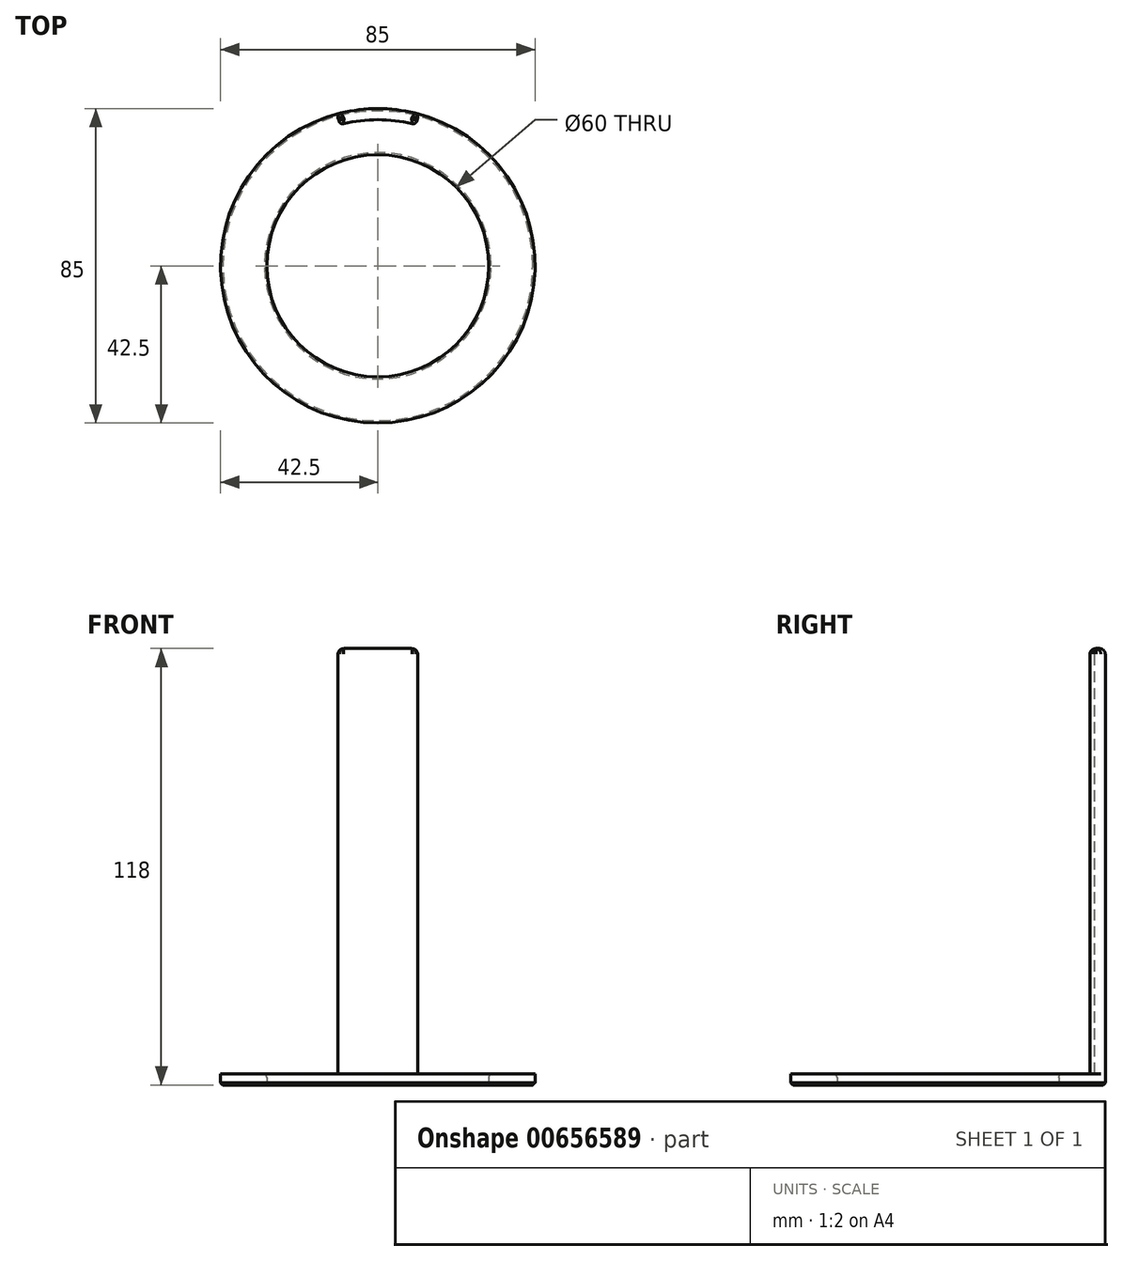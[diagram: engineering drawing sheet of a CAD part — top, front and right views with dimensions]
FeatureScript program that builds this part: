
annotation { "Feature Type Name" : "Feature", "Feature Type Description" : "" }
export const myFeature = defineFeature(function(context is Context, id is Id, definition is map)
    precondition{}
    {
        {
            var Q0;
            Q0=qCreatedBy(makeId("Front.planeOp"),FACE);
            var sketch = newSketch(context, id + "F0", { "sketchPlane" : qUnion([Q0])});
            skLineSegment(sketch, "E0", {"start": v(0, 0) * mm, "end": v(0, 66.8) * mm, "construction": true});
            skSolve(sketch);
        }
        {
            var Q0;
            Q0=qCreatedBy(makeId("Top.planeOp"),FACE);
            var sketch = newSketch(context, id + "F1", { "sketchPlane" : qUnion([Q0])});
            skCircle(sketch, "E1", {"center": v(0, 0) * mm, "radius": 42.5 * mm});
            skCircle(sketch, "E2", {"center": v(0, 0) * mm, "radius": 30 * mm});
            skSolve(sketch);
        }
        {
            var Q0;
            Q0=makeQuery(id+"F1.imprint","IMPRINT",FACE,{"disambiguationData":[TD([[makeQuery(id+"F1.imprint","IMPRINT",EDGE,{"derivedFrom":sQuery(id+"F1.wireOp",EDGE,"E1")}),1.0]])]});
            extrude(context, id + "F2", {"entities" : qUnion([Q0]), "depth" : 3 * mm, "offsetDistance" : 25 * mm});
        }
        {
            var Q0;
            Q0=makeQuery(id+"F2.opExtrude","CAP_EDGE",EDGE,{"disambiguationData":[OSD([sQuery(id+"F1.wireOp",EDGE,"E1")])],"isStart":true});
            var Q1;
            Q1=makeQuery(id+"F2.opExtrude","CAP_EDGE",EDGE,{"disambiguationData":[OSD([sQuery(id+"F1.wireOp",EDGE,"E2")])],"isStart":true});
            chamfer(context, id + "F3", {"entities" : qUnion([Q0, Q1]), "width" : 0.6 * mm, "tangentPropagation" : true});
        }
        {
            var Q0;
            Q0=makeQuery(id+"F2.opExtrude","CAP_EDGE",EDGE,{"disambiguationData":[OSD([sQuery(id+"F1.wireOp",EDGE,"E2")])],"isStart":false});
            fillet(context, id + "F4", {"entities" : qUnion([Q0]), "radius" : 1 * mm, "tangentPropagation" : true, "allowEdgeOverflow" : false});
        }
        {
            var Q0;
            Q0=makeQuery(id+"F2.opExtrude","CAP_FACE",FACE,{"disambiguationData":[OSD([sQuery(id+"F1.wireOp",EDGE,"E1"),sQuery(id+"F1.wireOp",EDGE,"E2")])],"isStart":false});
            var sketch = newSketch(context, id + "F5", { "sketchPlane" : qUnion([Q0])});
            skCircle(sketch, "E3.0", {"center": v(0, 0) * mm, "radius": 42.5 * mm});
            skCircle(sketch, "E4.0", {"center": v(0, 0) * mm, "radius": 39.5 * mm});
            skLineSegment(sketch, "E5", {"start": v(0, 0) * mm, "end": v(-11, 41.05) * mm});
            skLineSegment(sketch, "E6", {"start": v(0, 0) * mm, "end": v(11, 41.05) * mm});
            skLineSegment(sketch, "E7", {"start": v(0, 0) * mm, "end": v(0, 42.5) * mm, "construction": true});
            skSolve(sketch);
        }
        {
            var Q0;
            {var subQ0=sQuery(id+"F5.wireOp",EDGE,"E5");var subQ1=sQuery(id+"F5.wireOp",EDGE,"E3.0");var subQ2=makeQuery(id+"F5.imprint","INTERSECT",VERTEX,{"derivedFrom":[subQ1,subQ0]});Q0=makeQuery(id+"F5.imprint","IMPRINT",FACE,{"disambiguationData":[TD([[makeQuery(id+"F5.imprint","IMPRINT",EDGE,{"disambiguationData":[TD([[subQ2,1.0]])],"derivedFrom":subQ1}),1.0]])]});}
            extrude(context, id + "F6", {"entities" : qUnion([Q0]), "operationType" : NewBodyOperationType.ADD, "depth" : 115 * mm, "offsetDistance" : 25 * mm});
        }
        {
            var Q0;
            Q0=makeQuery(id+"F6.opExtrude","CAP_EDGE",EDGE,{"disambiguationData":[OSD([sQuery(id+"F5.wireOp",EDGE,"E4.0")])],"isStart":false});
            var Q1;
            Q1=makeQuery(id+"F6.opExtrude","CAP_EDGE",EDGE,{"disambiguationData":[OSD([sQuery(id+"F5.wireOp",EDGE,"E5")])],"isStart":false});
            var Q2;
            Q2=makeQuery(id+"F6.opExtrude","CAP_EDGE",EDGE,{"disambiguationData":[OSD([sQuery(id+"F5.wireOp",EDGE,"E3.0")])],"isStart":false});
            var Q3;
            Q3=makeQuery(id+"F6.opExtrude","CAP_EDGE",EDGE,{"disambiguationData":[OSD([sQuery(id+"F5.wireOp",EDGE,"E6")])],"isStart":false});
            fillet(context, id + "F7", {"entities" : qUnion([Q0, Q1, Q2, Q3]), "radius" : 1.5 * mm, "tangentPropagation" : true, "allowEdgeOverflow" : false});
        }
        {
            var Q0;
            Q0=makeQuery(id+"F6.opExtrude","SWEPT_EDGE",EDGE,{"disambiguationData":[OSD([sQuery(id+"F5.wireOp",EDGE,"E4.0"),sQuery(id+"F5.wireOp",EDGE,"E6")])]});
            var Q1;
            Q1=makeQuery(id+"F6.opExtrude","SWEPT_EDGE",EDGE,{"disambiguationData":[OSD([sQuery(id+"F5.wireOp",EDGE,"E4.0"),sQuery(id+"F5.wireOp",EDGE,"E5")])]});
            var Q2;
            Q2=makeQuery(id+"F6.opExtrude","SWEPT_EDGE",EDGE,{"disambiguationData":[OSD([sQuery(id+"F5.wireOp",EDGE,"E3.0"),sQuery(id+"F5.wireOp",EDGE,"E6")])]});
            var Q3;
            Q3=makeQuery(id+"F6.opExtrude","SWEPT_EDGE",EDGE,{"disambiguationData":[OSD([sQuery(id+"F5.wireOp",EDGE,"E3.0"),sQuery(id+"F5.wireOp",EDGE,"E5")])]});
            fillet(context, id + "F8", {"entities" : qUnion([Q0, Q1, Q2, Q3]), "radius" : 1 * mm, "tangentPropagation" : true, "allowEdgeOverflow" : false});
        }
    });
